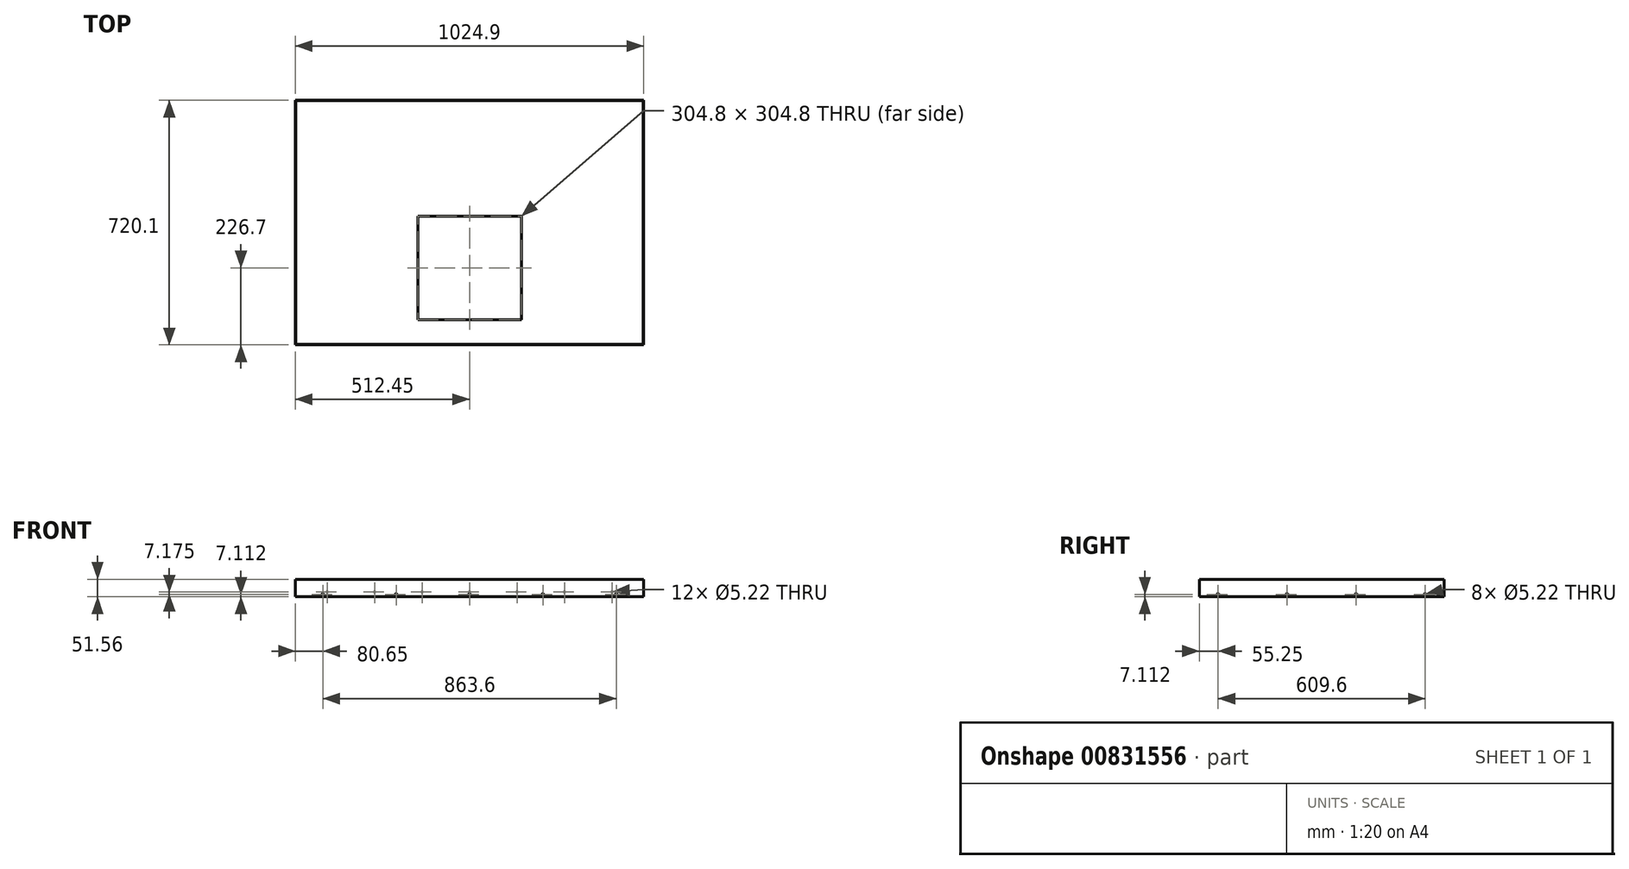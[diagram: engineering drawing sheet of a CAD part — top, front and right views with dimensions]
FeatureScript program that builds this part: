
annotation { "Feature Type Name" : "Feature", "Feature Type Description" : "" }
export const myFeature = defineFeature(function(context is Context, id is Id, definition is map)
    precondition{}
    {
        {
            var Q0;
            Q0=qCreatedBy(makeId("Top.planeOp"),FACE);
            var sketch = newSketch(context, id + "F0", { "sketchPlane" : qUnion([Q0])});
            skLineSegment(sketch, "E0", {"start": v(0, 360.04) * mm, "end": v(0, 0) * mm});
            skLineSegment(sketch, "E1", {"start": v(0, 0) * mm, "end": v(0, -360.04) * mm});
            skLineSegment(sketch, "E2.bottom", {"start": v(-512.45, 360.05) * mm, "end": v(512.45, 360.05) * mm});
            skLineSegment(sketch, "E2.top", {"start": v(-512.45, -360.05) * mm, "end": v(512.45, -360.05) * mm});
            skLineSegment(sketch, "E2.left", {"start": v(-512.45, 360.05) * mm, "end": v(-512.45, -360.05) * mm});
            skLineSegment(sketch, "E2.right", {"start": v(512.45, 360.05) * mm, "end": v(512.45, -360.05) * mm});
            skSolve(sketch);
        }
        {
            var Q0;
            Q0=qSketchRegion(id+"F0",true);
            extrude(context, id + "F1", {"entities" : qUnion([Q0]), "depth" : 51.56 * mm, "offsetDistance" : 25.4 * mm});
        }
        {
            var Q0;
            Q0=makeQuery(id+"F1.opExtrude","CAP_FACE",FACE,{"disambiguationData":[OSD([sQuery(id+"F0.wireOp",EDGE,"E2.bottom"),sQuery(id+"F0.wireOp",EDGE,"E2.top"),sQuery(id+"F0.wireOp",EDGE,"E2.left"),sQuery(id+"F0.wireOp",EDGE,"E2.right")])],"isStart":false});
            shell(context, id + "F2", {"entities" : qUnion([Q0]), "thickness" : 1.27 * mm});
        }
        {
            var Q0;
            Q0=makeQuery(id+"F1.opExtrude","SWEPT_FACE",FACE,{"disambiguationData":[OSD([sQuery(id+"F0.wireOp",EDGE,"E2.top")])]});
            var sketch = newSketch(context, id + "F3", { "sketchPlane" : qUnion([Q0])});
            skPoint(sketch, "E3", {"position": v(-431.8, 7.11) * mm});
            skPoint(sketch, "E4", {"position": v(-215.9, 7.11) * mm});
            skPoint(sketch, "E5", {"position": v(0, 7.11) * mm});
            skPoint(sketch, "E6", {"position": v(215.9, 7.11) * mm});
            skPoint(sketch, "E7", {"position": v(431.8, 7.11) * mm});
            skLineSegment(sketch, "E8", {"start": v(-431.8, 7.11) * mm, "end": v(-215.9, 7.11) * mm});
            skLineSegment(sketch, "E9", {"start": v(0, 7.11) * mm, "end": v(-215.9, 7.11) * mm});
            skLineSegment(sketch, "E10", {"start": v(0, 7.11) * mm, "end": v(215.9, 7.11) * mm});
            skLineSegment(sketch, "E11", {"start": v(215.9, 7.11) * mm, "end": v(431.8, 7.11) * mm});
            skLineSegment(sketch, "E12", {"start": v(0, 7.11) * mm, "end": v(0, 51.56) * mm});
            skSolve(sketch);
        }
        {
            var Q0;
            Q0=sQuery(id+"F3.wireOp",VERTEX,"E3");
            var Q1;
            Q1=sQuery(id+"F3.wireOp",VERTEX,"E4");
            var Q2;
            Q2=sQuery(id+"F3.wireOp",VERTEX,"E5");
            var Q3;
            Q3=sQuery(id+"F3.wireOp",VERTEX,"E6");
            var Q4;
            Q4=sQuery(id+"F3.wireOp",VERTEX,"E7");
            var Q5;
            Q5=makeQuery(id+"F1.opExtrude","SWEPT_BODY",BODY,{"disambiguationData":[OSD([sQuery(id+"F0.wireOp",EDGE,"E2.bottom"),sQuery(id+"F0.wireOp",EDGE,"E2.top"),sQuery(id+"F0.wireOp",EDGE,"E2.left"),sQuery(id+"F0.wireOp",EDGE,"E2.right")])]});
            hole(context, id + "F4", {"style" : HoleStyle.SIMPLE, "endStyle" : HoleEndStyle.BLIND, "standardTappedOrClearance" : lookupTablePath({ "standard" : "ANSI", "size" : "#5 (0.2)", "type" : "Drilled" }), "standardBlindInLast" : lookupTablePath({ "standard" : "ANSI", "size" : "#5 (0.2)", "type" : "Drilled" }), "holeDiameter" : 5.22 * mm, "majorDiameter" : 6.35 * mm, "holeDepth" : 0.76 * mm, "isTappedThrough" : true, "tappedDepth" : 12.7 * mm, "tapClearance" : 3, "locations" : qUnion([Q0, Q1, Q2, Q3, Q4]), "scope" : qUnion([Q5])});
        }
        {
            var Q0;
            Q0=makeQuery(id+"F1.opExtrude","SWEPT_FACE",FACE,{"disambiguationData":[OSD([sQuery(id+"F0.wireOp",EDGE,"E2.left")])]});
            var sketch = newSketch(context, id + "F5", { "sketchPlane" : qUnion([Q0])});
            skPoint(sketch, "E13", {"position": v(-304.8, 7.11) * mm});
            skPoint(sketch, "E14", {"position": v(-101.6, 7.11) * mm});
            skPoint(sketch, "E15", {"position": v(101.6, 7.11) * mm});
            skPoint(sketch, "E16", {"position": v(304.8, 7.11) * mm});
            skLineSegment(sketch, "E17", {"start": v(-304.8, 7.11) * mm, "end": v(-101.6, 7.11) * mm});
            skLineSegment(sketch, "E18", {"start": v(-101.6, 7.11) * mm, "end": v(101.6, 7.11) * mm});
            skLineSegment(sketch, "E19", {"start": v(101.6, 7.11) * mm, "end": v(304.8, 7.11) * mm});
            skLineSegment(sketch, "E20", {"start": v(0, 7.11) * mm, "end": v(0, 0) * mm});
            skSolve(sketch);
        }
        {
            var Q0;
            Q0=sQuery(id+"F5.wireOp",VERTEX,"E13");
            var Q1;
            Q1=sQuery(id+"F5.wireOp",VERTEX,"E14");
            var Q2;
            Q2=sQuery(id+"F5.wireOp",VERTEX,"E15");
            var Q3;
            Q3=sQuery(id+"F5.wireOp",VERTEX,"E16");
            var Q4;
            Q4=makeQuery(id+"F1.opExtrude","SWEPT_BODY",BODY,{"disambiguationData":[OSD([sQuery(id+"F0.wireOp",EDGE,"E2.bottom"),sQuery(id+"F0.wireOp",EDGE,"E2.top"),sQuery(id+"F0.wireOp",EDGE,"E2.left"),sQuery(id+"F0.wireOp",EDGE,"E2.right")])]});
            hole(context, id + "F6", {"style" : HoleStyle.SIMPLE, "endStyle" : HoleEndStyle.THROUGH, "standardTappedOrClearance" : lookupTablePath({ "standard" : "ANSI", "size" : "#5 (0.2)", "type" : "Drilled" }), "standardBlindInLast" : lookupTablePath({ "standard" : "ANSI", "size" : "#5 (0.2)", "type" : "Drilled" }), "holeDiameter" : 5.22 * mm, "majorDiameter" : 6.35 * mm, "isTappedThrough" : true, "tappedDepth" : 12.7 * mm, "tapClearance" : 3, "locations" : qUnion([Q0, Q1, Q2, Q3]), "scope" : qUnion([Q4])});
        }
        {
            var Q0;
            Q0=makeQuery(id+"F1.opExtrude","CAP_FACE",FACE,{"disambiguationData":[OSD([sQuery(id+"F0.wireOp",EDGE,"E2.bottom"),sQuery(id+"F0.wireOp",EDGE,"E2.top"),sQuery(id+"F0.wireOp",EDGE,"E2.left"),sQuery(id+"F0.wireOp",EDGE,"E2.right")])],"isStart":true});
            var sketch = newSketch(context, id + "F7", { "sketchPlane" : qUnion([Q0])});
            skLineSegment(sketch, "E21.bottom", {"start": v(-152.4, 285.75) * mm, "end": v(152.4, 285.75) * mm});
            skLineSegment(sketch, "E21.top", {"start": v(-152.4, -19.05) * mm, "end": v(152.4, -19.05) * mm});
            skLineSegment(sketch, "E21.left", {"start": v(-152.4, 285.75) * mm, "end": v(-152.4, -19.05) * mm});
            skLineSegment(sketch, "E21.right", {"start": v(152.4, 285.75) * mm, "end": v(152.4, -19.05) * mm});
            skLineSegment(sketch, "E22", {"start": v(-152.4, 133.35) * mm, "end": v(152.4, 133.35) * mm, "construction": true});
            skLineSegment(sketch, "E23", {"start": v(0, -19.05) * mm, "end": v(0, 285.75) * mm, "construction": true});
            skLineSegment(sketch, "E24", {"start": v(-512.45, 0) * mm, "end": v(0, 0) * mm, "construction": true});
            skLineSegment(sketch, "E25", {"start": v(0, 0) * mm, "end": v(512.45, 0) * mm, "construction": true});
            skSolve(sketch);
        }
        {
            var Q0;
            Q0=qSketchRegion(id+"F7",true);
            extrude(context, id + "F8", {"entities" : qUnion([Q0]), "operationType" : NewBodyOperationType.REMOVE, "oppositeDirection" : true, "depth" : 25.4 * mm, "offsetDistance" : 25.4 * mm});
        }
        {
            var Q0;
            Q0=makeQuery(id+"F1.opExtrude","SWEPT_FACE",FACE,{"disambiguationData":[OSD([sQuery(id+"F0.wireOp",EDGE,"E2.bottom")])]});
            var sketch = newSketch(context, id + "F9", { "sketchPlane" : qUnion([Q0])});
            skPoint(sketch, "E26", {"position": v(-419.1, 14.29) * mm});
            skPoint(sketch, "E27", {"position": v(-279.4, 14.29) * mm});
            skPoint(sketch, "E28", {"position": v(-139.7, 14.29) * mm});
            skPoint(sketch, "E29", {"position": v(0, 14.29) * mm});
            skPoint(sketch, "E30", {"position": v(139.7, 14.29) * mm});
            skPoint(sketch, "E31", {"position": v(279.4, 14.29) * mm});
            skPoint(sketch, "E32", {"position": v(419.1, 14.29) * mm});
            skLineSegment(sketch, "E33", {"start": v(-419.1, 14.29) * mm, "end": v(-279.4, 14.29) * mm, "construction": true});
            skLineSegment(sketch, "E34", {"start": v(-279.4, 14.29) * mm, "end": v(-139.7, 14.29) * mm, "construction": true});
            skLineSegment(sketch, "E35", {"start": v(-139.7, 14.29) * mm, "end": v(0, 14.29) * mm, "construction": true});
            skLineSegment(sketch, "E36", {"start": v(0, 14.29) * mm, "end": v(139.7, 14.29) * mm, "construction": true});
            skLineSegment(sketch, "E37", {"start": v(139.7, 14.29) * mm, "end": v(279.4, 14.29) * mm, "construction": true});
            skLineSegment(sketch, "E38", {"start": v(279.4, 14.29) * mm, "end": v(419.1, 14.29) * mm, "construction": true});
            skLineSegment(sketch, "E39", {"start": v(0, 0) * mm, "end": v(0, 14.29) * mm, "construction": true});
            skSolve(sketch);
        }
        {
            var Q0;
            Q0=sQuery(id+"F9.wireOp",VERTEX,"E26");
            var Q1;
            Q1=sQuery(id+"F9.wireOp",VERTEX,"E27");
            var Q2;
            Q2=sQuery(id+"F9.wireOp",VERTEX,"E28");
            var Q3;
            Q3=sQuery(id+"F9.wireOp",VERTEX,"E29");
            var Q4;
            Q4=sQuery(id+"F9.wireOp",VERTEX,"E30");
            var Q5;
            Q5=sQuery(id+"F9.wireOp",VERTEX,"E31");
            var Q6;
            Q6=sQuery(id+"F9.wireOp",VERTEX,"E32");
            var Q7;
            Q7=makeQuery(id+"F1.opExtrude","SWEPT_BODY",BODY,{"disambiguationData":[OSD([sQuery(id+"F0.wireOp",EDGE,"E2.bottom"),sQuery(id+"F0.wireOp",EDGE,"E2.top"),sQuery(id+"F0.wireOp",EDGE,"E2.left"),sQuery(id+"F0.wireOp",EDGE,"E2.right")])]});
            hole(context, id + "F10", {"style" : HoleStyle.SIMPLE, "endStyle" : HoleEndStyle.BLIND, "standardTappedOrClearance" : lookupTablePath({ "standard" : "ANSI", "size" : "#5 (0.2)", "type" : "Drilled" }), "standardBlindInLast" : lookupTablePath({ "standard" : "ANSI", "size" : "#5 (0.2)", "type" : "Drilled" }), "holeDiameter" : 5.22 * mm, "majorDiameter" : 6.35 * mm, "holeDepth" : 0.76 * mm, "isTappedThrough" : true, "tappedDepth" : 12.7 * mm, "tapClearance" : 3, "locations" : qUnion([Q0, Q1, Q2, Q3, Q4, Q5, Q6]), "scope" : qUnion([Q7])});
        }
    });
